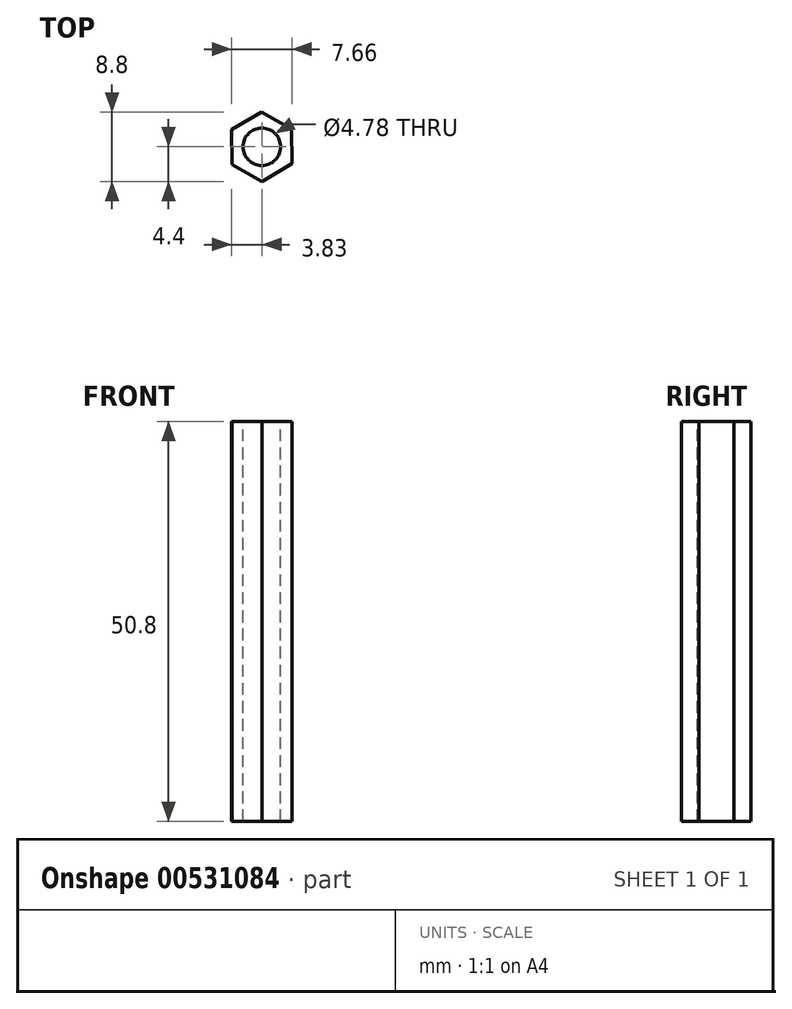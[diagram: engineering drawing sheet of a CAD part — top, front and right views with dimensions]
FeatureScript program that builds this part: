
annotation { "Feature Type Name" : "Feature", "Feature Type Description" : "" }
export const myFeature = defineFeature(function(context is Context, id is Id, definition is map)
    precondition{}
    {
        {
            var Q0;
            Q0=qCreatedBy(makeId("Top.planeOp"),FACE);
            var sketch = newSketch(context, id + "F0", { "sketchPlane" : qUnion([Q0])});
            skCircle(sketch, "E0.cCircle", {"center": v(0, 0) * mm, "radius": 3.8 * mm, "construction": true});
            skLineSegment(sketch, "E0.0", {"start": v(-0.05, 4.4) * mm, "end": v(3.79, 2.24) * mm});
            skLineSegment(sketch, "E0.1", {"start": v(3.79, 2.24) * mm, "end": v(3.83, -2.16) * mm});
            skLineSegment(sketch, "E0.2", {"start": v(3.83, -2.16) * mm, "end": v(0.05, -4.4) * mm});
            skLineSegment(sketch, "E0.3", {"start": v(0.05, -4.4) * mm, "end": v(-3.79, -2.24) * mm});
            skLineSegment(sketch, "E0.4", {"start": v(-3.79, -2.24) * mm, "end": v(-3.83, 2.16) * mm});
            skLineSegment(sketch, "E0.5", {"start": v(-3.83, 2.16) * mm, "end": v(-0.05, 4.4) * mm});
            skPoint(sketch, "E0.0.midPoint", {"position": v(1.87, 3.32) * mm});
            skSolve(sketch);
        }
        {
            var Q0;
            Q0=makeQuery(id+"F0.imprint","IMPRINT",FACE,{"disambiguationData":[TD([[makeQuery(id+"F0.imprint","IMPRINT",EDGE,{"derivedFrom":sQuery(id+"F0.wireOp",EDGE,"E0.0")}),-1.0]])]});
            extrude(context, id + "F1", {"entities" : qUnion([Q0]), "depth" : 50.8 * mm, "offsetDistance" : 25.4 * mm});
        }
        {
            var Q0;
            Q0=makeQuery(id+"F1.opExtrude","CAP_FACE",FACE,{"disambiguationData":[OSD([sQuery(id+"F0.wireOp",EDGE,"E0.0"),sQuery(id+"F0.wireOp",EDGE,"E0.1"),sQuery(id+"F0.wireOp",EDGE,"E0.2"),sQuery(id+"F0.wireOp",EDGE,"E0.3"),sQuery(id+"F0.wireOp",EDGE,"E0.4"),sQuery(id+"F0.wireOp",EDGE,"E0.5")])],"isStart":false});
            var sketch = newSketch(context, id + "F2", { "sketchPlane" : qUnion([Q0])});
            skCircle(sketch, "E1", {"center": v(0, 0) * mm, "radius": 2.39 * mm});
            skSolve(sketch);
        }
        {
            var Q0;
            Q0 = qSketchRegion(id + "F2", true);
            extrude(context, id + "F3", {"entities" : qUnion([Q0]), "operationType" : NewBodyOperationType.REMOVE, "oppositeDirection" : true, "depth" : 50.8 * mm, "offsetDistance" : 25.4 * mm});
        }
    });
